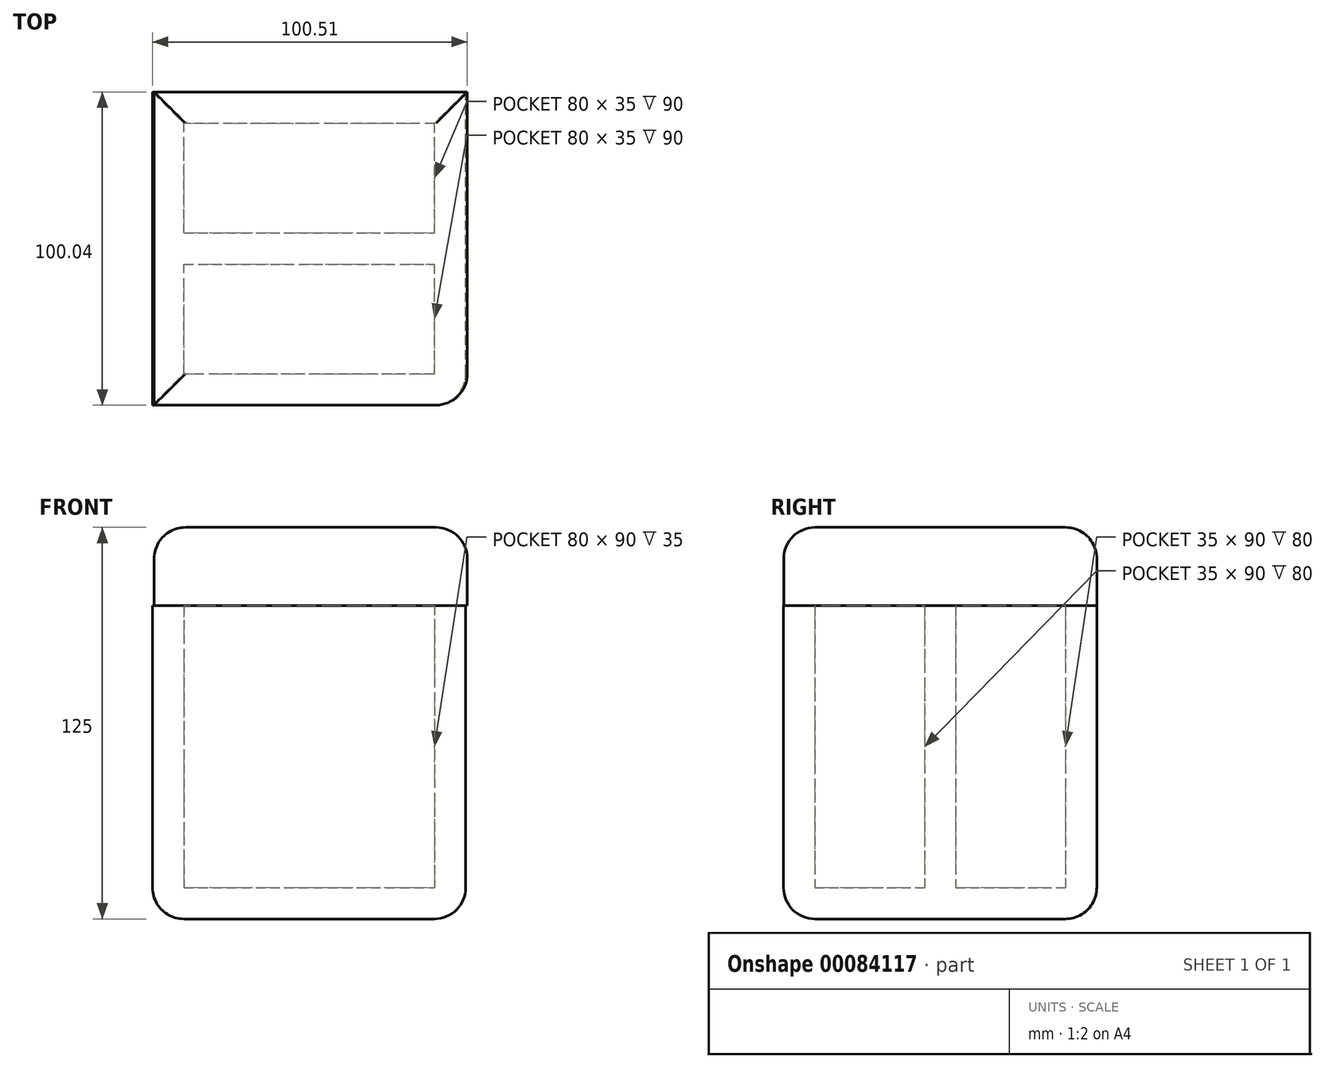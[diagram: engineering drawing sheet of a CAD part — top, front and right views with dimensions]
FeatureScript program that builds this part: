
annotation { "Feature Type Name" : "Feature", "Feature Type Description" : "" }
export const myFeature = defineFeature(function(context is Context, id is Id, definition is map)
    precondition{}
    {
        {
            var Q0;
            Q0=qCreatedBy(makeId("Top.planeOp"),FACE);
            var sketch = newSketch(context, id + "F0", { "sketchPlane" : qUnion([Q0])});
            skLineSegment(sketch, "E0.bottom", {"start": v(50, -50) * mm, "end": v(-50, -50) * mm});
            skLineSegment(sketch, "E0.top", {"start": v(50, 50) * mm, "end": v(-50, 50) * mm});
            skLineSegment(sketch, "E0.left", {"start": v(50, -50) * mm, "end": v(50, 50) * mm});
            skLineSegment(sketch, "E0.right", {"start": v(-50, -50) * mm, "end": v(-50, 50) * mm});
            skPoint(sketch, "E0.middle", {"position": v(0, 0) * mm});
            skSolve(sketch);
        }
        {
            var Q0;
            Q0=makeQuery(id+"F0.imprint","IMPRINT",FACE,{"disambiguationData":[TD([[makeQuery(id+"F0.imprint","IMPRINT",EDGE,{"derivedFrom":sQuery(id+"F0.wireOp",EDGE,"E0.bottom")}),-1.0]])]});
            extrude(context, id + "F1", {"entities" : qUnion([Q0]), "depth" : 100 * mm});
        }
        {
            var Q0;
            Q0=makeQuery(id+"F1.opExtrude","CAP_FACE",FACE,{"disambiguationData":[OSD([sQuery(id+"F0.wireOp",EDGE,"E0.bottom"),sQuery(id+"F0.wireOp",EDGE,"E0.top"),sQuery(id+"F0.wireOp",EDGE,"E0.left"),sQuery(id+"F0.wireOp",EDGE,"E0.right")])],"isStart":false});
            shell(context, id + "F2", {"entities" : qUnion([Q0]), "thickness" : 10 * mm});
        }
        {
            var Q0;
            Q0=qCreatedBy(makeId("Top.planeOp"),FACE);
            var sketch = newSketch(context, id + "F3", { "sketchPlane" : qUnion([Q0])});
            skLineSegment(sketch, "E1.bottom", {"start": v(40, 5) * mm, "end": v(-40, 5) * mm});
            skLineSegment(sketch, "E1.top", {"start": v(40, -5) * mm, "end": v(-40, -5) * mm});
            skLineSegment(sketch, "E1.left", {"start": v(40, 5) * mm, "end": v(40, -5) * mm});
            skLineSegment(sketch, "E1.right", {"start": v(-40, 5) * mm, "end": v(-40, -5) * mm});
            skPoint(sketch, "E1.middle", {"position": v(0, 0) * mm});
            skSolve(sketch);
        }
        {
            var Q0;
            Q0=makeQuery(id+"F3.imprint","IMPRINT",FACE,{"disambiguationData":[TD([[makeQuery(id+"F3.imprint","IMPRINT",EDGE,{"derivedFrom":sQuery(id+"F3.wireOp",EDGE,"E1.bottom")}),1.0]])]});
            extrude(context, id + "F4", {"entities" : qUnion([Q0]), "operationType" : NewBodyOperationType.ADD, "depth" : 100 * mm});
        }
        {
            var Q0;
            Q0=makeQuery(id+"F4.boolean.opBoolean","MERGE",FACE,{"derivedFrom":[makeQuery(id+"F1.opExtrude","CAP_FACE",FACE,{"disambiguationData":[OSD([sQuery(id+"F0.wireOp",EDGE,"E0.bottom"),sQuery(id+"F0.wireOp",EDGE,"E0.top"),sQuery(id+"F0.wireOp",EDGE,"E0.left"),sQuery(id+"F0.wireOp",EDGE,"E0.right")])],"isStart":false}),makeQuery(id+"F4.opExtrude","CAP_FACE",FACE,{"disambiguationData":[OSD([sQuery(id+"F3.wireOp",EDGE,"E1.bottom"),sQuery(id+"F3.wireOp",EDGE,"E1.top"),sQuery(id+"F3.wireOp",EDGE,"E1.left"),sQuery(id+"F3.wireOp",EDGE,"E1.right")])],"isStart":false})]});
            cPlane(context, id + "F5", {"entities" : qUnion([Q0]), "cplaneType" : CPlaneType.OFFSET, "offset" : 0 * mm, "width" : 150 * mm, "height" : 150 * mm});
        }
        {
            var Q0;
            Q0=qCreatedBy(id+"F5.planeOp",FACE);
            var sketch = newSketch(context, id + "F6", { "sketchPlane" : qUnion([Q0])});
            skLineSegment(sketch, "E2.bottom", {"start": v(-49.49, 50.04) * mm, "end": v(50.51, 50.04) * mm});
            skLineSegment(sketch, "E2.top", {"start": v(-49.49, -49.96) * mm, "end": v(50.51, -49.96) * mm});
            skLineSegment(sketch, "E2.left", {"start": v(-49.49, 50.04) * mm, "end": v(-49.49, -49.96) * mm});
            skLineSegment(sketch, "E2.right", {"start": v(50.51, 50.04) * mm, "end": v(50.51, -49.96) * mm});
            skSolve(sketch);
        }
        {
            var Q0;
            Q0 = qSketchRegion(id + "F6", true);
            extrude(context, id + "F7", {"entities" : qUnion([Q0]), "operationType" : NewBodyOperationType.ADD, "depth" : 25 * mm});
        }
        {
            var Q0;
            Q0=makeQuery(id+"F7.opExtrude","CAP_FACE",FACE,{"disambiguationData":[OSD([sQuery(id+"F6.wireOp",EDGE,"E2.bottom"),sQuery(id+"F6.wireOp",EDGE,"E2.top"),sQuery(id+"F6.wireOp",EDGE,"E2.left"),sQuery(id+"F6.wireOp",EDGE,"E2.right")])],"isStart":false});
            fillet(context, id + "F8", {"entities" : qUnion([Q0]), "radius" : 10 * mm, "tangentPropagation" : true, "allowEdgeOverflow" : false});
        }
        {
            var Q0;
            Q0=makeQuery(id+"F1.opExtrude","CAP_FACE",FACE,{"disambiguationData":[OSD([sQuery(id+"F0.wireOp",EDGE,"E0.bottom"),sQuery(id+"F0.wireOp",EDGE,"E0.top"),sQuery(id+"F0.wireOp",EDGE,"E0.left"),sQuery(id+"F0.wireOp",EDGE,"E0.right")])],"isStart":true});
            fillet(context, id + "F9", {"entities" : qUnion([Q0]), "radius" : 10 * mm, "tangentPropagation" : true, "allowEdgeOverflow" : false});
        }
        {
            var Q0;
            Q0=makeQuery(id+"F1.opExtrude","SWEPT_EDGE",EDGE,{"disambiguationData":[OSD([sQuery(id+"F0.wireOp",EDGE,"E0.bottom"),sQuery(id+"F0.wireOp",EDGE,"E0.left")])]});
            fillet(context, id + "F10", {"entities" : qUnion([Q0]), "radius" : 10 * mm, "tangentPropagation" : true, "allowEdgeOverflow" : false});
        }
        {
            var Q0;
            Q0=makeQuery(id+"F7.opExtrude","SWEPT_EDGE",EDGE,{"disambiguationData":[OSD([sQuery(id+"F6.wireOp",EDGE,"E2.top"),sQuery(id+"F6.wireOp",EDGE,"E2.right")])]});
            fillet(context, id + "F11", {"entities" : qUnion([Q0]), "radius" : 10 * mm, "tangentPropagation" : true, "allowEdgeOverflow" : false});
        }
    });
